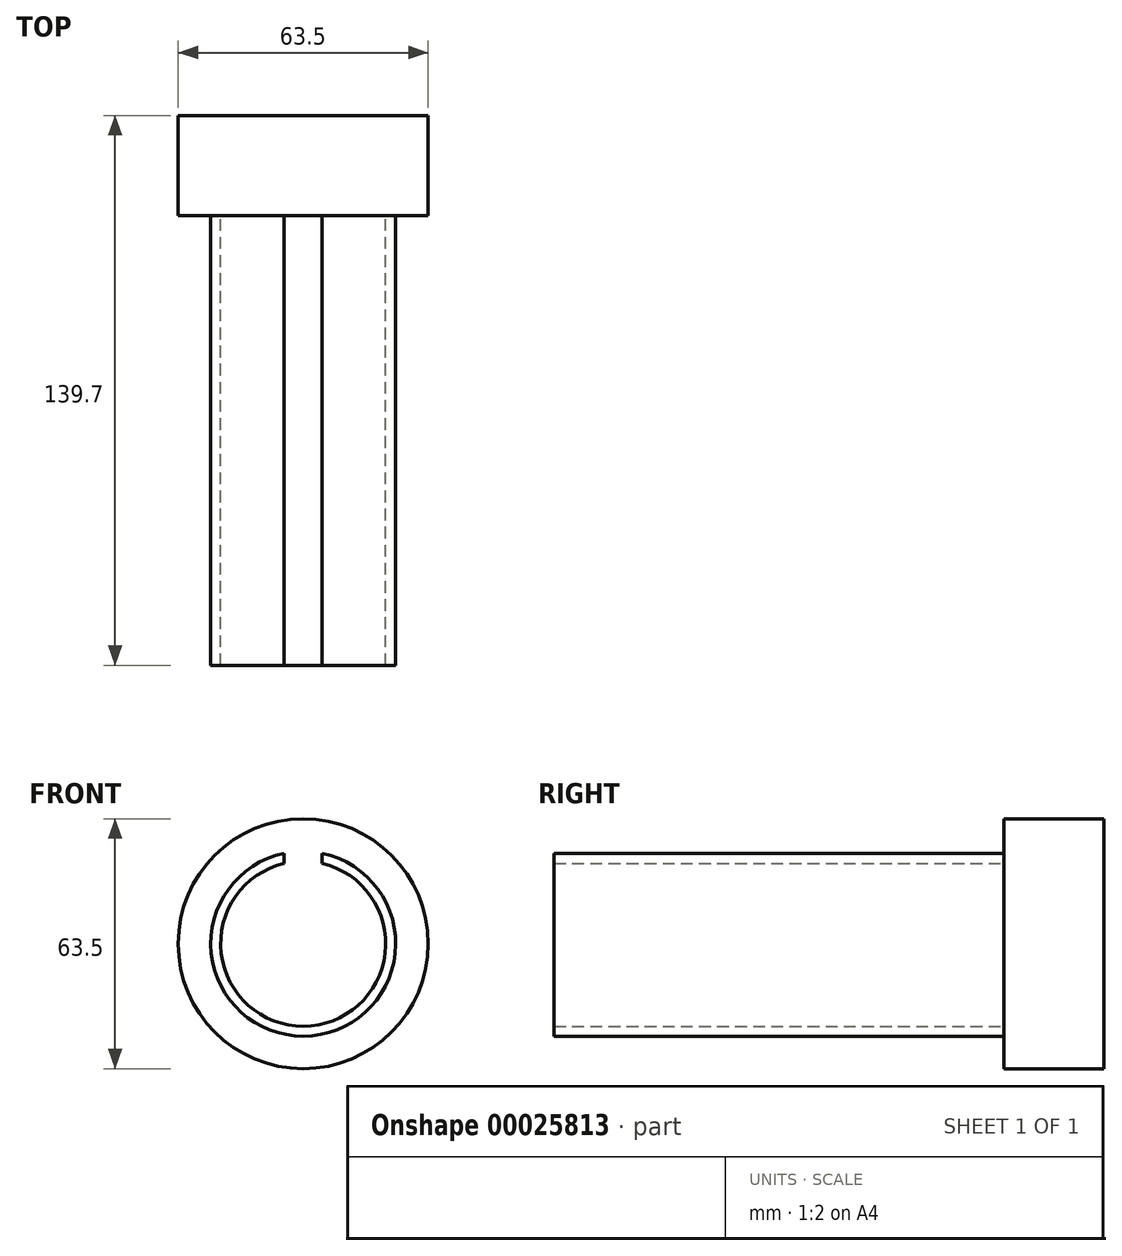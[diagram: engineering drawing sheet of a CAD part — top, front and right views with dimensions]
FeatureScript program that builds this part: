
annotation { "Feature Type Name" : "Feature", "Feature Type Description" : "" }
export const myFeature = defineFeature(function(context is Context, id is Id, definition is map)
    precondition{}
    {
        {
            var Q0;
            Q0=qCreatedBy(makeId("Front.planeOp"),FACE);
            var sketch = newSketch(context, id + "F0", { "sketchPlane" : qUnion([Q0])});
            skCircle(sketch, "E0", {"center": v(0, 0) * mm, "radius": 31.75 * mm});
            skSolve(sketch);
        }
        {
            var Q0;
            Q0=makeQuery(id+"F0.imprint","IMPRINT",FACE,{"disambiguationData":[TD([[makeQuery(id+"F0.imprint","IMPRINT",EDGE,{"derivedFrom":sQuery(id+"F0.wireOp",EDGE,"E0")}),1.0]])]});
            extrude(context, id + "F1", {"entities" : qUnion([Q0]), "depth" : 25.4 * mm});
        }
        {
            var Q0;
            Q0=makeQuery(id+"F1.opExtrude","CAP_FACE",FACE,{"disambiguationData":[OSD([sQuery(id+"F0.wireOp",EDGE,"E0")])],"isStart":false});
            var sketch = newSketch(context, id + "F2", { "sketchPlane" : qUnion([Q0])});
            skArc(sketch, "E1", {"start": v(-4.83, 23) * mm, "mid": v(0, -23.5) * mm, "end": v(4.83, 23) * mm});
            skArc(sketch, "E2", {"start": v(-4.83, 20.4) * mm, "mid": v(0, -20.97) * mm, "end": v(4.83, 20.4) * mm});
            skLineSegment(sketch, "E3", {"start": v(-4.83, 20.4) * mm, "end": v(-4.83, 23) * mm});
            skLineSegment(sketch, "E4", {"start": v(4.83, 20.4) * mm, "end": v(4.83, 23) * mm});
            skSolve(sketch);
        }
        {
            var Q0;
            Q0=makeQuery(id+"F2.imprint","IMPRINT",FACE,{"disambiguationData":[TD([[makeQuery(id+"F2.imprint","IMPRINT",EDGE,{"derivedFrom":sQuery(id+"F2.wireOp",EDGE,"E1")}),1.0]])]});
            extrude(context, id + "F3", {"entities" : qUnion([Q0]), "operationType" : NewBodyOperationType.ADD, "depth" : 114.3 * mm});
        }
    });
